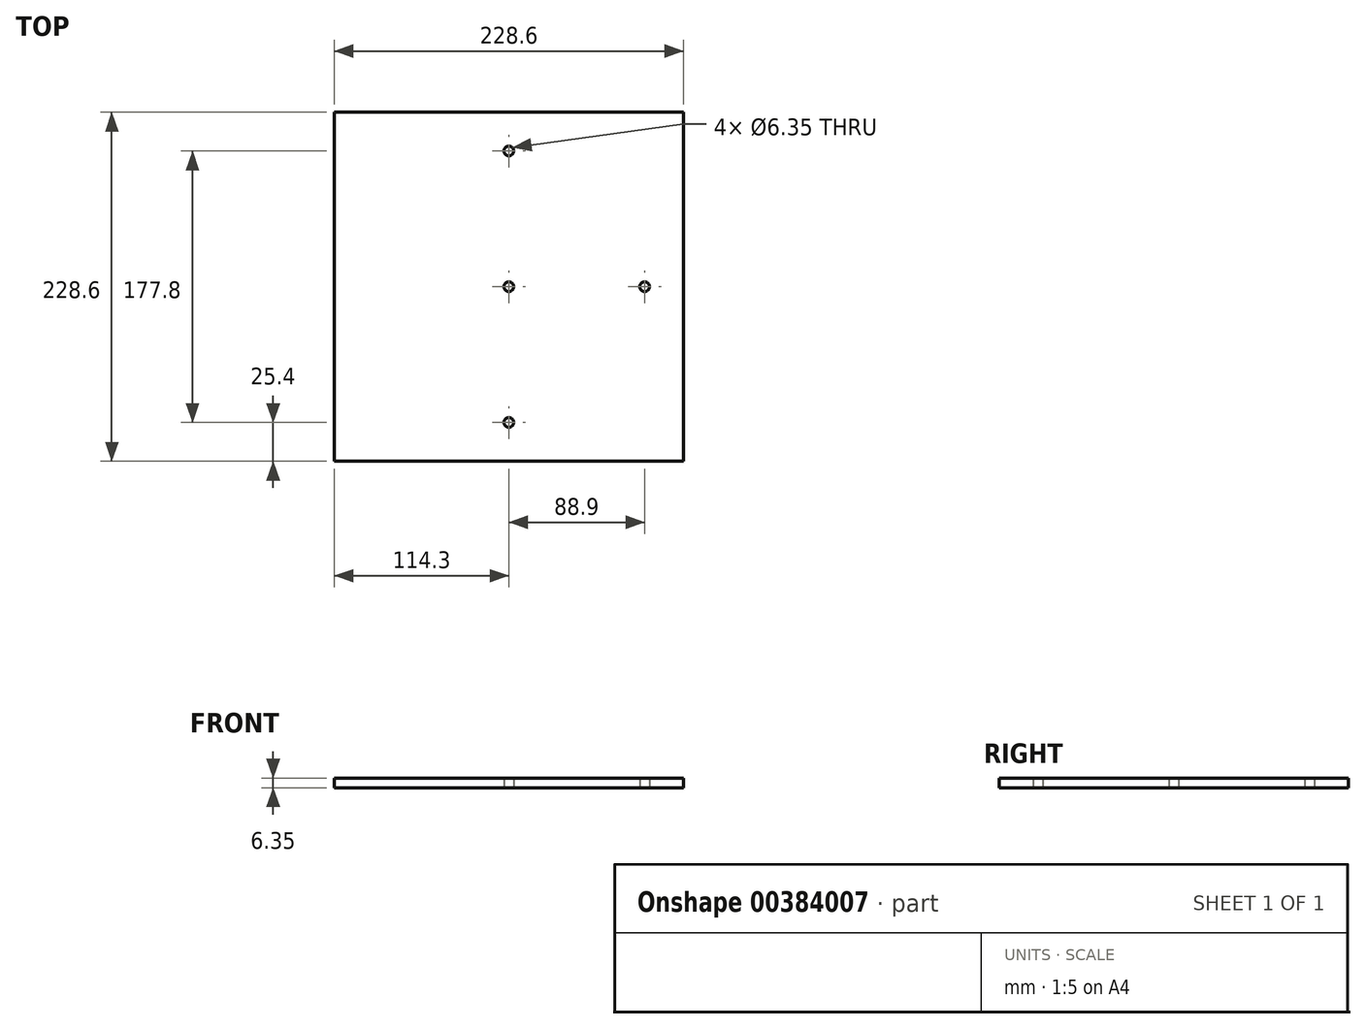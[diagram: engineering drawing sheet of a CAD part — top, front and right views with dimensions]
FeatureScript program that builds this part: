
annotation { "Feature Type Name" : "Feature", "Feature Type Description" : "" }
export const myFeature = defineFeature(function(context is Context, id is Id, definition is map)
    precondition{}
    {
        {
            var Q0;
            Q0=qCreatedBy(makeId("Top.planeOp"),FACE);
            var sketch = newSketch(context, id + "F0", { "sketchPlane" : qUnion([Q0])});
            skLineSegment(sketch, "E0.bottom", {"start": v(0, 0) * mm, "end": v(228.6, 0) * mm});
            skLineSegment(sketch, "E0.top", {"start": v(0, 228.6) * mm, "end": v(228.6, 228.6) * mm});
            skLineSegment(sketch, "E0.left", {"start": v(0, 0) * mm, "end": v(0, 228.6) * mm});
            skLineSegment(sketch, "E0.right", {"start": v(228.6, 0) * mm, "end": v(228.6, 228.6) * mm});
            skCircle(sketch, "E1", {"center": v(114.3, 203.2) * mm, "radius": 3.18 * mm});
            skCircle(sketch, "E2", {"center": v(203.2, 114.3) * mm, "radius": 3.18 * mm});
            skCircle(sketch, "E3", {"center": v(114.3, 25.4) * mm, "radius": 3.18 * mm});
            skCircle(sketch, "E4", {"center": v(114.3, 114.3) * mm, "radius": 3.18 * mm});
            skSolve(sketch);
        }
        {
            var Q0;
            Q0=makeQuery(id+"F0.imprint","IMPRINT",FACE,{"disambiguationData":[TD([[makeQuery(id+"F0.imprint","IMPRINT",EDGE,{"derivedFrom":sQuery(id+"F0.wireOp",EDGE,"E0.bottom")}),1.0]])]});
            extrude(context, id + "F1", {"entities" : qUnion([Q0]), "depth" : 6.35 * mm});
        }
    });
